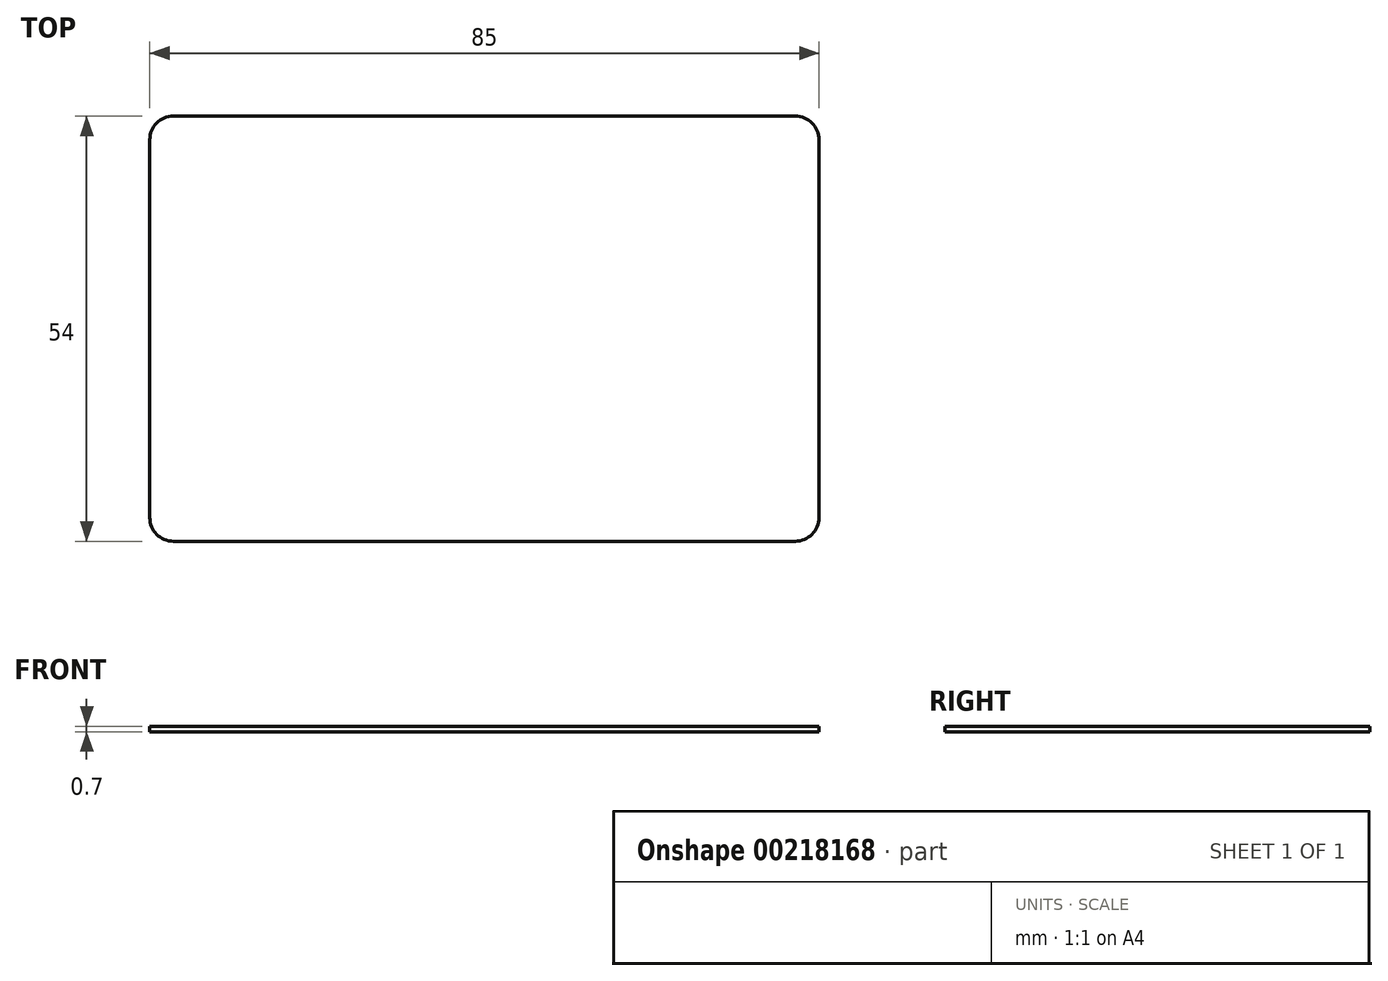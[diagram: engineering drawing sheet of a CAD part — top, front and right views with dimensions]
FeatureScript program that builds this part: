
annotation { "Feature Type Name" : "Feature", "Feature Type Description" : "" }
export const myFeature = defineFeature(function(context is Context, id is Id, definition is map)
    precondition{}
    {
        {
            var Q0;
            Q0=qCreatedBy(makeId("Top.planeOp"),FACE);
            var sketch = newSketch(context, id + "F0", { "sketchPlane" : qUnion([Q0])});
            skLineSegment(sketch, "E0.bottom", {"start": v(39.5, -27) * mm, "end": v(-39.5, -27) * mm});
            skLineSegment(sketch, "E0.top", {"start": v(39.5, 27) * mm, "end": v(-39.5, 27) * mm});
            skLineSegment(sketch, "E0.left", {"start": v(42.5, -24) * mm, "end": v(42.5, 24) * mm});
            skLineSegment(sketch, "E0.right", {"start": v(-42.5, -24) * mm, "end": v(-42.5, 24) * mm});
            skPoint(sketch, "E0.middle", {"position": v(0, 0) * mm});
            skPoint(sketch, "E1.visualSharp", {"position": v(-42.5, 27) * mm});
            skArc(sketch, "E1.filletArc", {"start": v(-39.5, 27) * mm, "mid": v(-41.62, 26.12) * mm, "end": v(-42.5, 24) * mm});
            skPoint(sketch, "E2.visualSharp", {"position": v(-42.5, -27) * mm});
            skArc(sketch, "E2.filletArc", {"start": v(-42.5, -24) * mm, "mid": v(-41.62, -26.12) * mm, "end": v(-39.5, -27) * mm});
            skPoint(sketch, "E3.visualSharp", {"position": v(42.5, -27) * mm});
            skArc(sketch, "E3.filletArc", {"start": v(39.5, -27) * mm, "mid": v(41.62, -26.12) * mm, "end": v(42.5, -24) * mm});
            skPoint(sketch, "E4.visualSharp", {"position": v(42.5, 27) * mm});
            skArc(sketch, "E4.filletArc", {"start": v(42.5, 24) * mm, "mid": v(41.62, 26.12) * mm, "end": v(39.5, 27) * mm});
            skSolve(sketch);
        }
        {
            var Q0;
            Q0=makeQuery(id+"F0.imprint","IMPRINT",FACE,{"disambiguationData":[TD([[makeQuery(id+"F0.imprint","IMPRINT",EDGE,{"derivedFrom":sQuery(id+"F0.wireOp",EDGE,"E0.bottom")}),-1.0]])]});
            extrude(context, id + "F1", {"entities" : qUnion([Q0]), "depth" : .7 * mm});
        }
    });
